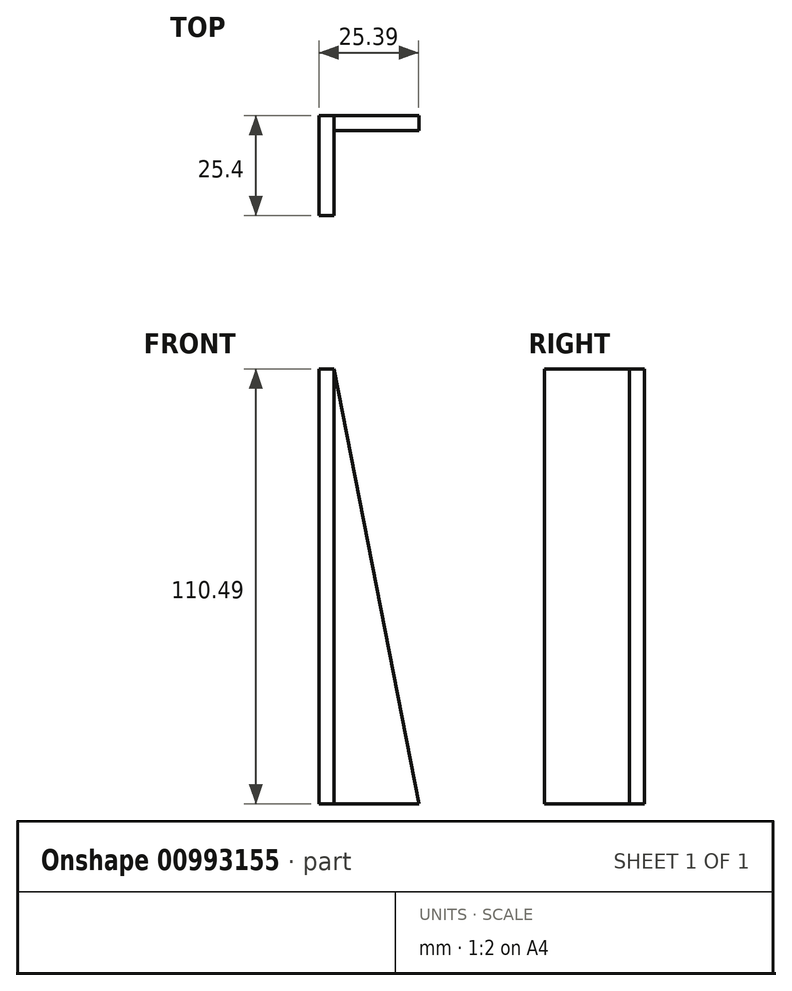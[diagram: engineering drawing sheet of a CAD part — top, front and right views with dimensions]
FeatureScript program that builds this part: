
annotation { "Feature Type Name" : "Feature", "Feature Type Description" : "" }
export const myFeature = defineFeature(function(context is Context, id is Id, definition is map)
    precondition{}
    {
        {
            var Q0;
            Q0=qCreatedBy(makeId("Front.planeOp"),FACE);
            var sketch = newSketch(context, id + "F0", { "sketchPlane" : qUnion([Q0])});
            skLineSegment(sketch, "E0", {"start": v(-44.82, 63.34) * mm, "end": v(-44.82, -47.15) * mm});
            skLineSegment(sketch, "E1", {"start": v(-44.82, -47.15) * mm, "end": v(-19.43, -47.15) * mm});
            skLineSegment(sketch, "E2", {"start": v(-19.43, -47.15) * mm, "end": v(-44.82, 63.34) * mm});
            skLineSegment(sketch, "E3.bottom", {"start": v(-19.43, -47.15) * mm, "end": v(-44.82, -47.15) * mm});
            skLineSegment(sketch, "E3.top", {"start": v(-19.43, 63.34) * mm, "end": v(-44.82, 63.34) * mm});
            skLineSegment(sketch, "E3.left", {"start": v(-19.43, -47.15) * mm, "end": v(-19.43, 63.34) * mm});
            skLineSegment(sketch, "E3.right", {"start": v(-44.82, -47.15) * mm, "end": v(-44.82, 63.34) * mm});
            skSolve(sketch);
        }
        {
            var Q0;
            Q0=makeQuery(id+"F0.imprint","IMPRINT",FACE,{"disambiguationData":[TD([[makeQuery(id+"F0.imprint","IMPRINT",EDGE,{"derivedFrom":sQuery(id+"F0.wireOp",EDGE,"E0")}),1.0]])]});
            var Q1;
            Q1=makeQuery(id+"F0.imprint","IMPRINT",FACE,{"disambiguationData":[TD([[makeQuery(id+"F0.imprint","IMPRINT",EDGE,{"derivedFrom":sQuery(id+"F0.wireOp",EDGE,"E2")}),-1.0]])]});
            var Q2;
            Q2=makeQuery(id+"F0.imprint","IMPRINT",FACE,{"disambiguationData":[TD([[makeQuery(id+"F0.imprint","IMPRINT",EDGE,{"derivedFrom":sQuery(id+"F0.wireOp",EDGE,"E2")}),1.0]])]});
            extrude(context, id + "F1", {"entities" : qUnion([Q0, Q1, Q2]), "depth" : 25.4 * mm, "offsetDistance" : 25.4 * mm});
        }
        {
            var Q0;
            Q0=makeQuery(id+"F1.opExtrude","SWEPT_FACE",FACE,{"disambiguationData":[OSD([sQuery(id+"F0.wireOp",EDGE,"E3.top")])]});
            var sketch = newSketch(context, id + "F2", { "sketchPlane" : qUnion([Q0])});
            skLineSegment(sketch, "E4.bottom", {"start": v(-19.43, -25.4) * mm, "end": v(-41, -25.4) * mm});
            skLineSegment(sketch, "E4.top", {"start": v(-19.43, -3.81) * mm, "end": v(-41, -3.81) * mm});
            skLineSegment(sketch, "E4.left", {"start": v(-19.43, -25.4) * mm, "end": v(-19.43, -3.81) * mm});
            skLineSegment(sketch, "E4.right", {"start": v(-41, -25.4) * mm, "end": v(-41, -3.81) * mm});
            skSolve(sketch);
        }
        {
            var Q0;
            Q0=makeQuery(id+"F2.imprint","IMPRINT",FACE,{"disambiguationData":[TD([[makeQuery(id+"F2.imprint","IMPRINT",EDGE,{"derivedFrom":sQuery(id+"F2.wireOp",EDGE,"E4.bottom")}),-1.0]])]});
            extrude(context, id + "F3", {"entities" : qUnion([Q0]), "operationType" : NewBodyOperationType.REMOVE, "oppositeDirection" : true, "depth" : 127 * mm, "offsetDistance" : 25.4 * mm});
        }
        {
            var Q0;
            Q0=makeQuery(id+"F3.boolean.opBoolean","COPY",FACE,{"derivedFrom":makeQuery(id+"F3.opExtrude","SWEPT_FACE",FACE,{"disambiguationData":[OSD([sQuery(id+"F2.wireOp",EDGE,"E4.top")])]})});
            var sketch = newSketch(context, id + "F4", { "sketchPlane" : qUnion([Q0])});
            skLineSegment(sketch, "E5", {"start": v(-41, 63.34) * mm, "end": v(-19.43, -47.15) * mm});
            skSolve(sketch);
        }
        {
            var Q0;
            Q0=makeQuery(id+"F4.imprint","IMPRINT",FACE,{"disambiguationData":[TD([[makeQuery(id+"F4.imprint","IMPRINT",EDGE,{"derivedFrom":sQuery(id+"F4.wireOp",EDGE,"E5")}),1.0]])]});
            extrude(context, id + "F5", {"entities" : qUnion([Q0]), "operationType" : NewBodyOperationType.REMOVE, "oppositeDirection" : true, "depth" : 25.4 * mm, "offsetDistance" : 25.4 * mm});
        }
    });
